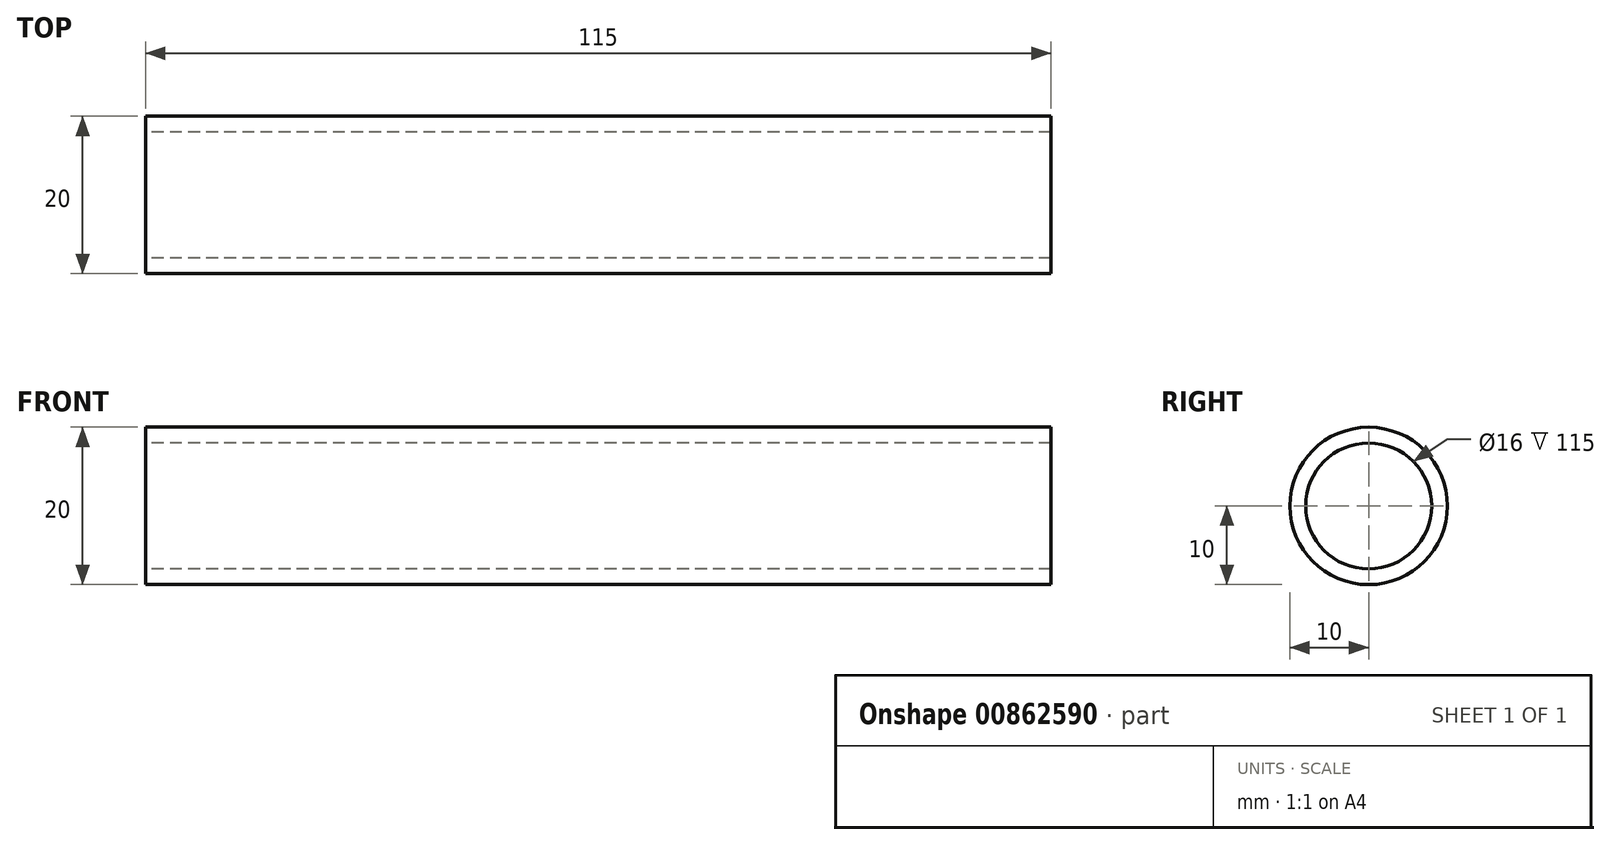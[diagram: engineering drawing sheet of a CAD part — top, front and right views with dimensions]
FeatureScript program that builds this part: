
annotation { "Feature Type Name" : "Feature", "Feature Type Description" : "" }
export const myFeature = defineFeature(function(context is Context, id is Id, definition is map)
    precondition{}
    {
        {
            var Q0;
            Q0=qCreatedBy(makeId("Front.planeOp"),FACE);
            var sketch = newSketch(context, id + "F0", { "sketchPlane" : qUnion([Q0])});
            skLineSegment(sketch, "E0", {"start": v(0, 0) * mm, "end": v(-115, 0) * mm});
            skSolve(sketch);
        }
        {
            var Q0;
            Q0=qCreatedBy(makeId("Right.planeOp"),FACE);
            var sketch = newSketch(context, id + "F1", { "sketchPlane" : qUnion([Q0])});
            skCircle(sketch, "E1", {"center": v(0, 0) * mm, "radius": 10 * mm});
            skCircle(sketch, "E2.0", {"center": v(0, 0) * mm, "radius": 8 * mm});
            skSolve(sketch);
        }
        {
            var Q0;
            Q0=makeQuery(id+"F1.imprint","IMPRINT",FACE,{"disambiguationData":[TD([[makeQuery(id+"F1.imprint","IMPRINT",EDGE,{"derivedFrom":sQuery(id+"F1.wireOp",EDGE,"E1")}),1.0]])]});
            var Q1;
            Q1=qSketchRegion(id+"F0",true);
            var Q2;
            Q2=sQuery(id+"F0.wireOp",EDGE,"E0");
            var Q3;
            Q3=sQuery(id+"F0.wireOp",EDGE,"p5A3UMdK-bUuJ-hKgG-gMdl-WLMVe5IsXQ4y");
            var Q4;
            Q4=sQuery(id+"F0.wireOp",EDGE,"jqzmJtes-IEFJ-0xae-phxS-a4aVOckqLKgL");
            sweep(context, id + "F2", {"profiles" : qUnion([Q0, Q1]), "path" : qUnion([Q2, Q3, Q4])});
        }
    });
